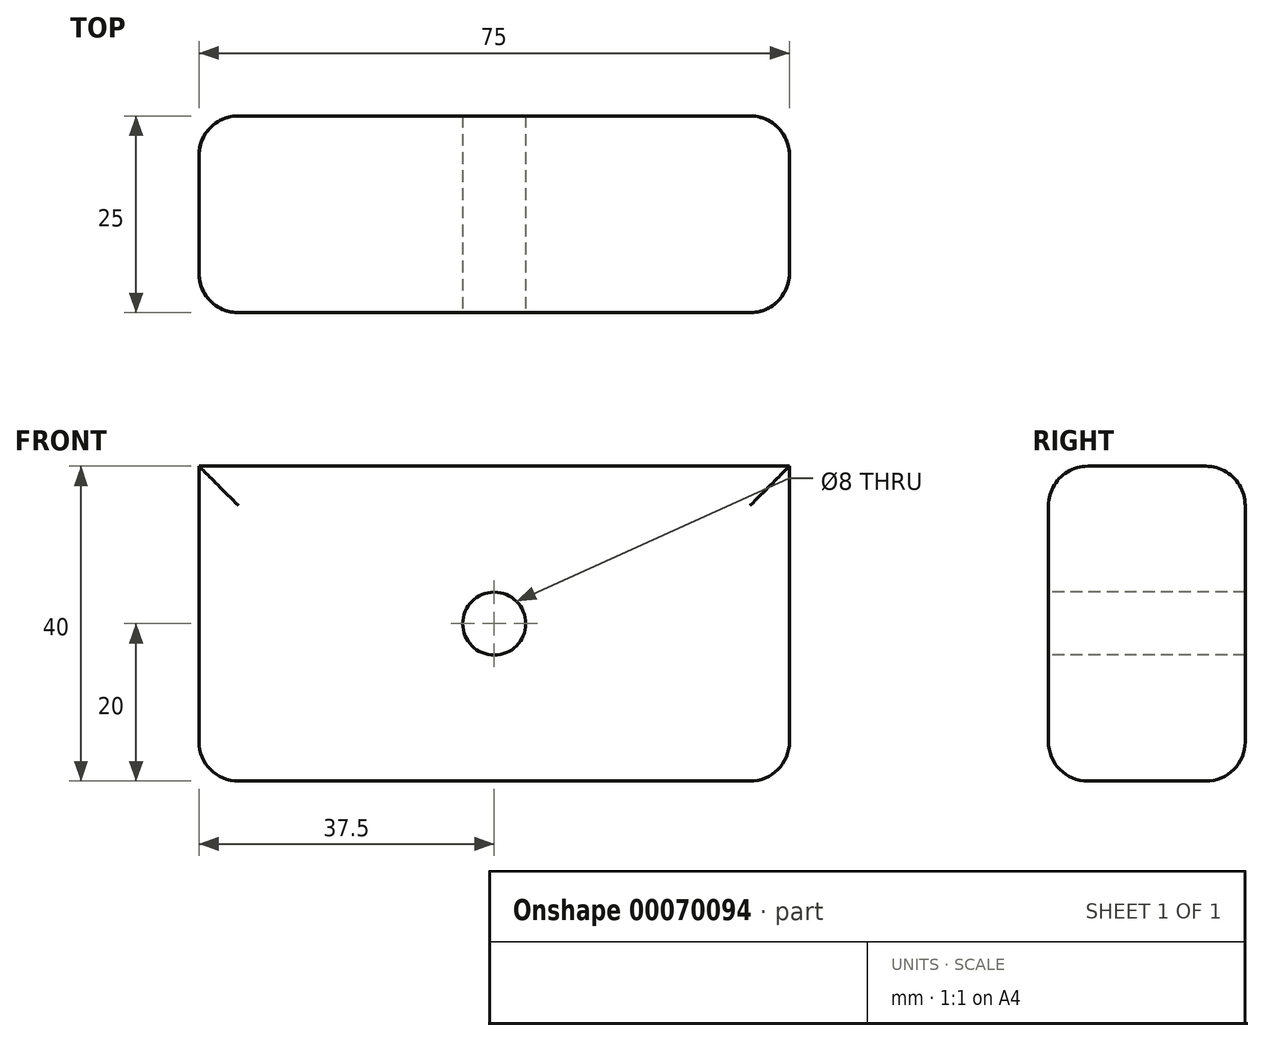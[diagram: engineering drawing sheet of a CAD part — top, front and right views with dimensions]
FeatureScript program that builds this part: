
annotation { "Feature Type Name" : "Feature", "Feature Type Description" : "" }
export const myFeature = defineFeature(function(context is Context, id is Id, definition is map)
    precondition{}
    {
        {
            var Q0;
            Q0=qCreatedBy(makeId("Front.planeOp"),FACE);
            var sketch = newSketch(context, id + "F0", { "sketchPlane" : qUnion([Q0])});
            skLineSegment(sketch, "E0.rect.bottom", {"start": v(37.5, 20) * mm, "end": v(-37.5, 20) * mm});
            skLineSegment(sketch, "E0.rect.top", {"start": v(37.5, -20) * mm, "end": v(-37.5, -20) * mm});
            skLineSegment(sketch, "E0.rect.left", {"start": v(37.5, 20) * mm, "end": v(37.5, -20) * mm});
            skLineSegment(sketch, "E0.rect.right", {"start": v(-37.5, 20) * mm, "end": v(-37.5, -20) * mm});
            skPoint(sketch, "E0.rect.middle", {"position": v(0, 0) * mm});
            skSolve(sketch);
        }
        {
            var Q0;
            Q0 = qSketchRegion(id + "F0", true);
            extrude(context, id + "F1", {"entities" : qUnion([Q0]), "depth" : 25 * mm});
        }
        {
            var Q0;
            Q0=makeQuery(id+"F1.opExtrude","CAP_FACE",FACE,{"disambiguationData":[OSD([sQuery(id+"F0.wireOp",EDGE,"E0.rect.bottom"),sQuery(id+"F0.wireOp",EDGE,"E0.rect.top"),sQuery(id+"F0.wireOp",EDGE,"E0.rect.left"),sQuery(id+"F0.wireOp",EDGE,"E0.rect.right")])],"isStart":false});
            var sketch = newSketch(context, id + "F2", { "sketchPlane" : qUnion([Q0])});
            skCircle(sketch, "E1", {"center": v(0, 0) * mm, "radius": 4 * mm});
            skSolve(sketch);
        }
        {
            var Q0;
            Q0=makeQuery(id+"F2.imprint","IMPRINT",FACE,{"disambiguationData":[TD([[makeQuery(id+"F2.imprint","IMPRINT",EDGE,{"derivedFrom":sQuery(id+"F2.wireOp",EDGE,"E1")}),1.0]])]});
            extrude(context, id + "F3", {"entities" : qUnion([Q0]), "operationType" : NewBodyOperationType.REMOVE, "oppositeDirection" : true, "depth" : 25 * mm});
        }
        {
            var Q0;
            Q0=makeQuery(id+"F1.opExtrude","CAP_EDGE",EDGE,{"disambiguationData":[OSD([sQuery(id+"F0.wireOp",EDGE,"E0.rect.bottom")])],"isStart":false});
            var Q1;
            Q1=makeQuery(id+"F1.opExtrude","CAP_EDGE",EDGE,{"disambiguationData":[OSD([sQuery(id+"F0.wireOp",EDGE,"E0.rect.right")])],"isStart":false});
            var Q2;
            Q2=makeQuery(id+"F1.opExtrude","CAP_EDGE",EDGE,{"disambiguationData":[OSD([sQuery(id+"F0.wireOp",EDGE,"E0.rect.top")])],"isStart":false});
            var Q3;
            Q3=makeQuery(id+"F1.opExtrude","CAP_EDGE",EDGE,{"disambiguationData":[OSD([sQuery(id+"F0.wireOp",EDGE,"E0.rect.left")])],"isStart":false});
            fillet(context, id + "F4", {"entities" : qUnion([Q0, Q1, Q2, Q3]), "radius" : 5 * mm, "tangentPropagation" : true, "allowEdgeOverflow" : false});
        }
        {
            var Q0;
            Q0=makeQuery(id+"F3.boolean.opBoolean","COPY",EDGE,{"derivedFrom":makeQuery(id+"F3.opExtrude","CAP_EDGE",EDGE,{"disambiguationData":[OSD([sQuery(id+"F2.wireOp",EDGE,"E1")])],"isStart":true})});
            var Q1;
            Q1=makeQuery(id+"F1.opExtrude","SWEPT_FACE",FACE,{"disambiguationData":[OSD([sQuery(id+"F0.wireOp",EDGE,"E0.rect.top")])]});
            var Q2;
            Q2=makeQuery(id+"F1.opExtrude","CAP_EDGE",EDGE,{"disambiguationData":[OSD([sQuery(id+"F0.wireOp",EDGE,"E0.rect.left")])],"isStart":true});
            var Q3;
            Q3=makeQuery(id+"F1.opExtrude","CAP_EDGE",EDGE,{"disambiguationData":[OSD([sQuery(id+"F0.wireOp",EDGE,"E0.rect.top")])],"isStart":true});
            var Q4;
            Q4=makeQuery(id+"F1.opExtrude","CAP_EDGE",EDGE,{"disambiguationData":[OSD([sQuery(id+"F0.wireOp",EDGE,"E0.rect.right")])],"isStart":true});
            var Q5;
            Q5=makeQuery(id+"F1.opExtrude","CAP_EDGE",EDGE,{"disambiguationData":[OSD([sQuery(id+"F0.wireOp",EDGE,"E0.rect.bottom")])],"isStart":true});
            fillet(context, id + "F5", {"entities" : qUnion([Q0, Q1, Q2, Q3, Q4, Q5]), "radius" : 5 * mm, "tangentPropagation" : true, "allowEdgeOverflow" : false});
        }
    });
